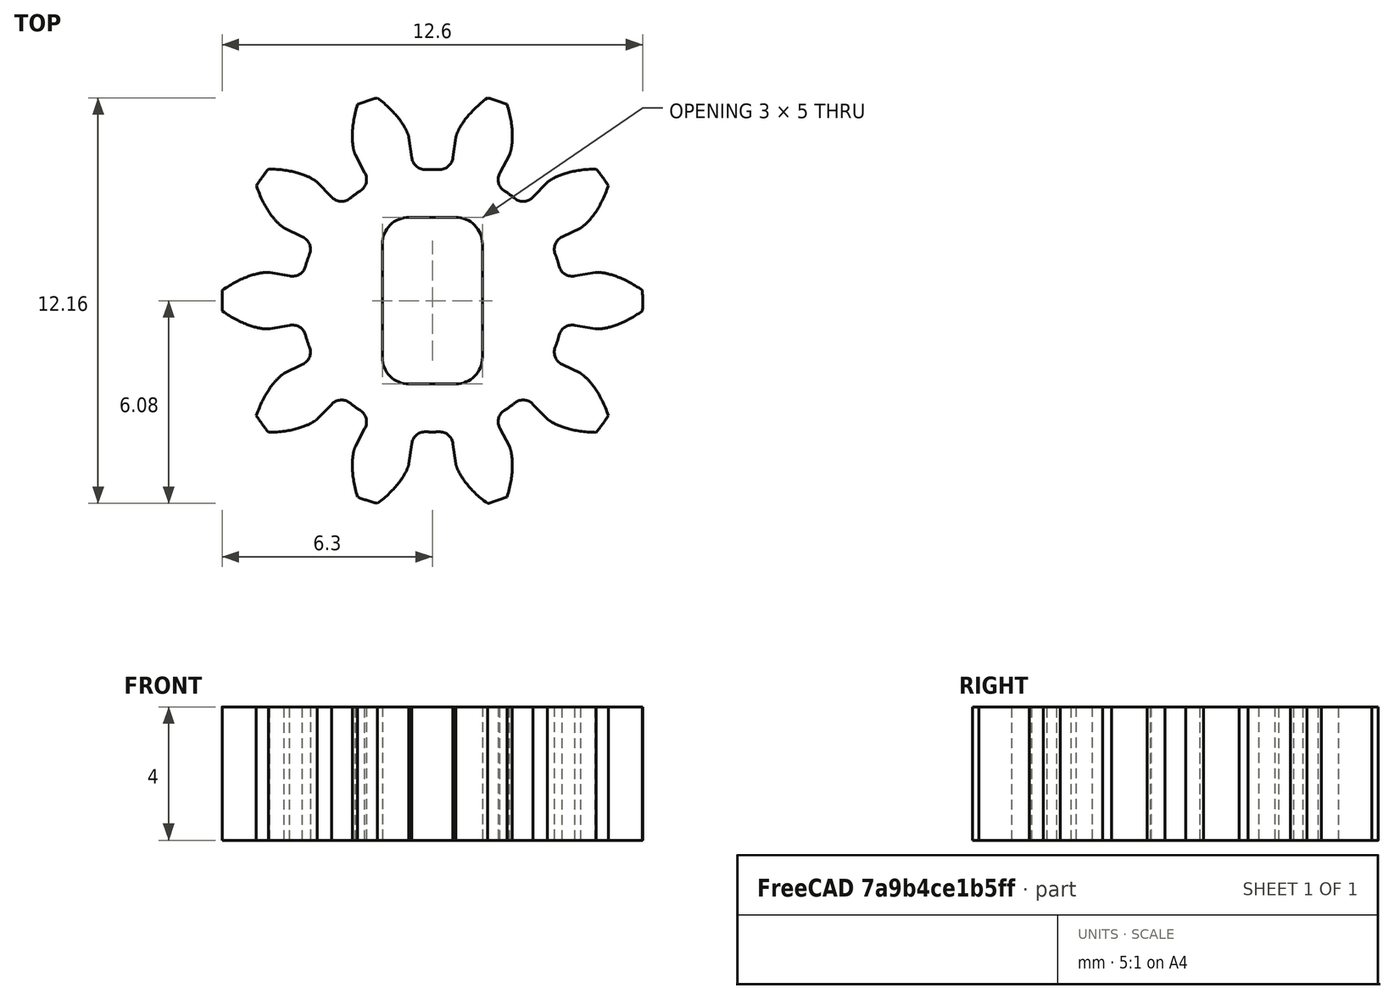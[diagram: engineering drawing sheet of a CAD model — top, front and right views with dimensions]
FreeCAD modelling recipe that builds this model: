
FCSTD DOCUMENT  (FreeCAD 1.0R39109 (Git))
Label: pignon
License: All rights reserved
LicenseURL: https://en.wikipedia.org/wiki/All_rights_reserved
objects: Sketcher::SketchObject×2, Part::Part2DObjectPython×1, PartDesign::Pad×1, PartDesign::Pocket×1, PartDesign::Fillet×1, Mesh::Feature×1, PartDesign::CoordinateSystem×1, PartDesign::Body×1
note: 16 computed .brp shape members not serialized (recipe doc carries the construction recipe); baked Part::Feature solids carry a one-line shape summary decoded from their .brp

FEATURE [Sketcher::SketchObject] Sketch
  ArcFitTolerance = 0
  AttachmentSupport = -> [XY_Plane]
  FullyConstrained = true
  MakeInternals = false
  MapMode = 5
  sketch-geometry (1):
    g0: Circle CenterX=0 CenterY=0 CenterZ=0 NormalX=0 NormalY=0 NormalZ=1 AngleXU=0 Radius=6.5
  constraints (2):
    c: Coincident(g0,g-1)
    c: Diameter(g0) = 13
FEATURE [Part::Part2DObjectPython] InvoluteGear  # Draft 2D object (typed FeaturePython)
  AddendumCoefficient = 1
  DedendumCoefficient = 1.25
  ExternalGear = true
  HighPrecision = true
  Modules = 1.05
  NumberOfTeeth = 10
  PressureAngle = 20
  ProfileShiftCoefficient = 0
  RootFilletCoefficient = 0.38
FEATURE [PartDesign::Pad] Pad
  Direction = (0,0,1)
  Length = 4
  Length2 = 10
  Profile = -> InvoluteGear
  ReferenceAxis = -> InvoluteGear [N_Axis]
  Suppressed = false
  Type = 0
FEATURE [Sketcher::SketchObject] Sketch001
  ArcFitTolerance = 0
  AttachmentSupport = -> [Pad]
  FullyConstrained = true
  MakeInternals = false
  MapMode = 5
  Placement = pos=(0,0,4) rot=(0,0,1;0rad)
  sketch-geometry (5):
    g0: LineSegment StartX=-1.5 StartY=-2.5 StartZ=0 EndX=-1.5 EndY=2.5 EndZ=0
    g1: LineSegment StartX=-1.5 StartY=2.5 StartZ=0 EndX=1.5 EndY=2.5 EndZ=0
    g2: LineSegment StartX=1.5 StartY=2.5 StartZ=0 EndX=1.5 EndY=-2.5 EndZ=0
    g3: LineSegment StartX=1.5 StartY=-2.5 StartZ=0 EndX=-1.5 EndY=-2.5 EndZ=0
    g4: GeomPoint [constr] X=0 Y=0 Z=0
  constraints (12):
    c: Coincident(g0,g1)
    c: Coincident(g1,g2)
    c: Coincident(g2,g3)
    c: Coincident(g3,g0)
    c: Horizontal(g1)
    c: Horizontal(g3)
    c: Vertical(g0)
    c: Vertical(g2)
    c: Symmetric(g1,g0,g4)
    c: Coincident(g4,g-1)
    c: Distance(g2) = 5
    c: Distance(g1) = 3
FEATURE [PartDesign::Pocket] Pocket
  BaseFeature = -> Pad
  Direction = (0,0,-1)
  Length = 5
  Length2 = 5
  Profile = -> Sketch001
  ReferenceAxis = -> Sketch001 [N_Axis]
  Suppressed = false
  Type = 1
FEATURE [PartDesign::Fillet] Fillet
  Base = -> Pocket [Edge310,Edge311,Edge312,Edge309]
  BaseFeature = -> Pocket
  Radius = 0.8
  SupportTransform = false
  Suppressed = false
  UseAllEdges = false
FEATURE [Mesh::Feature] Mesh  label="Corps (Meshed)"
FEATURE [PartDesign::CoordinateSystem] LCS_1
  AttacherType = Attacher::AttachEngine3D
  AttachmentSupport = -> [Fillet]
  MapMode = 5
  Placement = pos=(0,0,4) rot=(0,0,1;0rad)
FEATURE [PartDesign::Body] Body  label="pignon"
  AllowCompound = false
  Group = -> [Sketch,InvoluteGear,Pad,Sketch001,Pocket,Fillet,LCS_1]
  Origin = -> Origin
  Tip = -> Fillet
